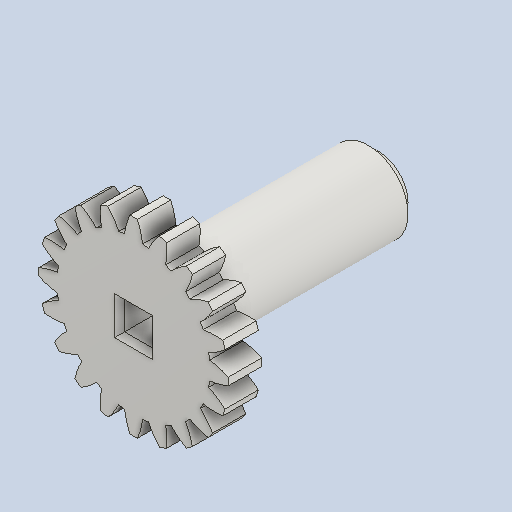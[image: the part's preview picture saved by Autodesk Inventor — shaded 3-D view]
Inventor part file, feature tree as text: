
AUTODESK INVENTOR PART (.ipt)
format: ipt  version: 2022 (Build 260153000, 153)  size: 277,504 bytes
history: native  units: in
note: dims shown in document units (in); Inventor stores cm internally (conversion verified against a paired STEP export)
features: other x12, sketch x4, plane x3
ambient origin geometry x8: Origin, YZ Plane, XZ Plane, XY Plane, X Axis, Y Axis, Z Axis, Center Point
bodies: Solid1 (feature_tree)
feature tree (19):
  other  "Spur Gear2"
  other  "Solid1::Spur Gear2"
  other  "TaggingFeature1"
  sketch  "Sketch1"  dims[d0=0.3937in]
  sketch  "Sketch2"  dims[d9=0.0in]
  sketch  "Sketch3"  dims[d14=0.0in]
  sketch  "Sketch4"  dims[d15=1.0in d16=0.0in d17=0.0in d18=0.0in d19=1.0in]
  plane  "XZ Plane_1"
  plane  "Work Plane2"
  plane  "Work Plane3"
  other  "Srf1"
  other  "Srf1::Derived"
  other  "Start plane iMate"
  other  "Distance iMate"
  other  "Position iMate"
  other  "Mesh iMate"
  other  "Axis iMate"
  other  "Mesh iMate2"
  other  "Align iMate"
